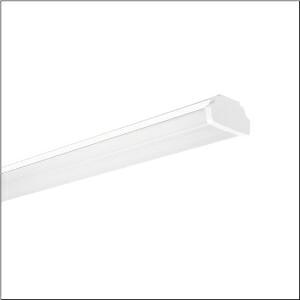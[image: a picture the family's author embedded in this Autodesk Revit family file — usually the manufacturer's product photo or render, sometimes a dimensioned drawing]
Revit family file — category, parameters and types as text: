
# Revit family: modario_r__31_ho_53bm812d2v4120_42ed
name_source: partatom
category: Lighting Fixtures
units: mm (PartAtom-declared; Revit-internal decimal feet)

## family parameters
Cut with Voids When Loaded = No
Host = Face
Light Source = No
Part Type = Normal
Room Calculation Point = No
Round Connector Dimension = Use Diameter
Shared = No

## types (1)
- --- (1 x LED, 12350 lm, 79.5 W, 4000K)
    Apparent Load = 80 VA
    CIE Flux Codes = 47 80 95 92 100
    Color Rendering = 80
    Color Temperature = 4000K
    Default Elevation = 1800 mm
    Description = Modario® 31 HO, luminaire insert, of sheet steel, coil coated, white, length: 1.495mm, width: 81mm, height: 82mm, 5x system unit, system units: 299mm, LED rated luminous flux: 12.350lm, light colour: 840, control gear: DALI 2, control gear: ECG DALI, with plug, 5-pole, with phase selection, mains connection: 220..240V, AC, 50/60Hz, rated input power: 80W, through-wiring accessed according to module size, primary optical cover: cover, of PMMA, light emission: direct distribution, primary light characteristic: symmetric, protection rating (complete): IP20, protection rating (LED compartment): IP50, insulation class (complete): insulation class I (protective earthing), certification: CE, ENEC, VDE, UKCA, impact resistance: IK03, permissible ambient temperature for indoor applications: -25..+30°C, corresponds to IFS (International Featured Standards) requirements for safety and quality in the food industry, reducing of maximum allowable ambient temperature of 5°C with ceiling mounting, packaging unit: 1 piece
    Height = 92 mm
    Lamp = 1 x LED
    Lamp Light Flux = 12350 lm
    Lamp Power = 79.5 W
    Lamp count = 1
    Length = 1495 mm
    Luminous efficacy = 155 lm/W
    Manufacturer = Siteco
    ModVariant = No
    Model = 53BM812D2V4120
    Mounting Place = Ceiling
    Mounting Type = Pendant
    Number of Poles = 1
    OnlyDefault = Yes
    Power Factor = 1
    Product Name = Modario® 31 HO
    Product group = luminaire insert
    ProductGroupID = 901
    Protection Class = Protection class I
    Protection Degree = IP 20
    RLX_Detail_Level = 1
    RLX_Emergency_Light_Flux = 0 lm
    RLX_Emergency_Type = 0
    RLX_Emergency_Type_DB = No
    RlxData = <blob elided: 42277 chars, md5=ef74a937>
    Socket = socket
    Standby Power = 0 W
    System Light Flux = 12350 lm
    System Power = 80 W
    Type Comments = factory setting: luminous flux: 100 % | dim-lin: 254 | 345 mA
    Type Image = l_1300283.jpg
    URL = http://relux.com
    VarID = @adj_156173
    Voltage = 0 V
    Weight = 0.00 kg
    Width = 81 mm

## geometry (parser evidence)
native form markers: Blend x4, Sweep x11
no freeform markers — native parametric forms only
